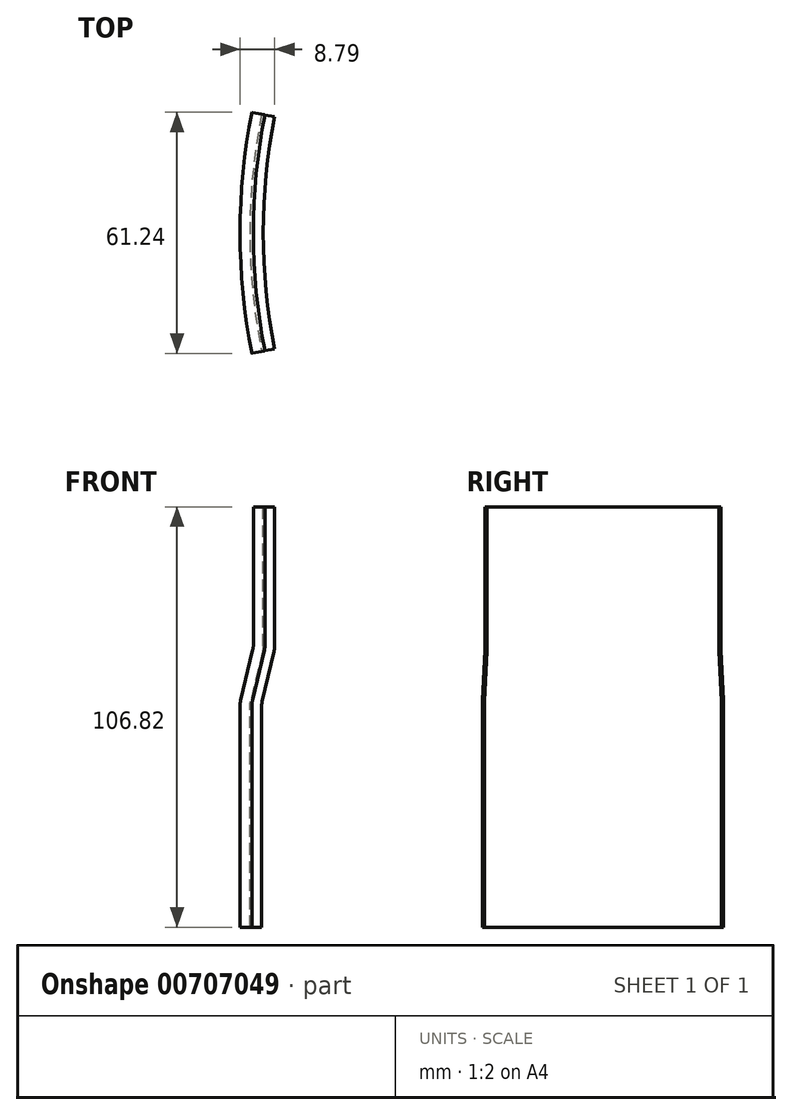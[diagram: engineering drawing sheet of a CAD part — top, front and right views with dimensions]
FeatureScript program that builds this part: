
annotation { "Feature Type Name" : "Feature", "Feature Type Description" : "" }
export const myFeature = defineFeature(function(context is Context, id is Id, definition is map)
    precondition{}
    {
        {
            var Q0;
            Q0=qCreatedBy(makeId("Front.planeOp"),FACE);
            var sketch = newSketch(context, id + "F0", { "sketchPlane" : qUnion([Q0])});
            skLineSegment(sketch, "E0", {"start": v(-153.55, 22.25) * mm, "end": v(-153.55, 57.25) * mm});
            skLineSegment(sketch, "E1", {"start": v(-155.55, 24.43) * mm, "end": v(-155.55, 20.43) * mm});
            skLineSegment(sketch, "E2", {"start": v(-153.71, 20.85) * mm, "end": v(-156.76, 8.1) * mm});
            skLineSegment(sketch, "E3", {"start": v(-156.93, 6.7) * mm, "end": v(-156.93, -49.57) * mm});
            skLineSegment(sketch, "E4.0", {"start": v(-151.05, 21.95) * mm, "end": v(-151.05, 57.25) * mm});
            skLineSegment(sketch, "E4.1", {"start": v(-151.21, 20.55) * mm, "end": v(-154.26, 7.8) * mm});
            skLineSegment(sketch, "E4.2", {"start": v(-154.43, 6.4) * mm, "end": v(-154.43, -49.57) * mm});
            skPoint(sketch, "E5.visualSharp", {"position": v(-156.93, 7.4) * mm});
            skArc(sketch, "E5.filletArc", {"start": v(-156.76, 8.1) * mm, "mid": v(-156.89, 7.4) * mm, "end": v(-156.93, 6.7) * mm});
            skPoint(sketch, "E6.visualSharp", {"position": v(-154.43, 7.11) * mm});
            skArc(sketch, "E6.filletArc", {"start": v(-154.26, 7.8) * mm, "mid": v(-154.39, 7.1) * mm, "end": v(-154.43, 6.4) * mm});
            skPoint(sketch, "E7.visualSharp", {"position": v(-151.05, 21.24) * mm});
            skArc(sketch, "E7.filletArc", {"start": v(-151.21, 20.55) * mm, "mid": v(-151.09, 21.25) * mm, "end": v(-151.05, 21.95) * mm});
            skPoint(sketch, "E8.visualSharp", {"position": v(-153.55, 21.54) * mm});
            skArc(sketch, "E8.filletArc", {"start": v(-153.71, 20.85) * mm, "mid": v(-153.59, 21.54) * mm, "end": v(-153.55, 22.25) * mm});
            skLineSegment(sketch, "E9", {"start": v(-154.43, -49.57) * mm, "end": v(-156.93, -49.57) * mm});
            skLineSegment(sketch, "E10", {"start": v(-151.05, 57.25) * mm, "end": v(-153.55, 57.25) * mm});
            skLineSegment(sketch, "E11", {"start": v(0, 72.16) * mm, "end": v(0, -90.96) * mm, "construction": true});
            skSolve(sketch);
        }
        {
            var Q0;
            Q0=makeQuery(id+"F0.imprint","IMPRINT",FACE,{"disambiguationData":[TD([[makeQuery(id+"F0.imprint","IMPRINT",EDGE,{"derivedFrom":sQuery(id+"F0.wireOp",EDGE,"E0")}),-1.0]])]});
            var Q1;
            Q1=sQuery(id+"F0.wireOp",EDGE,"E11");
            revolve(context, id + "F1", {"surfaceOperationType" : NewSurfaceOperationType.NEW, "entities" : qUnion([Q0]), "axis" : qUnion([Q1]), "revolveType" : RevolveType.SYMMETRIC, "angle" : 22.5 * degree});
        }
    });
